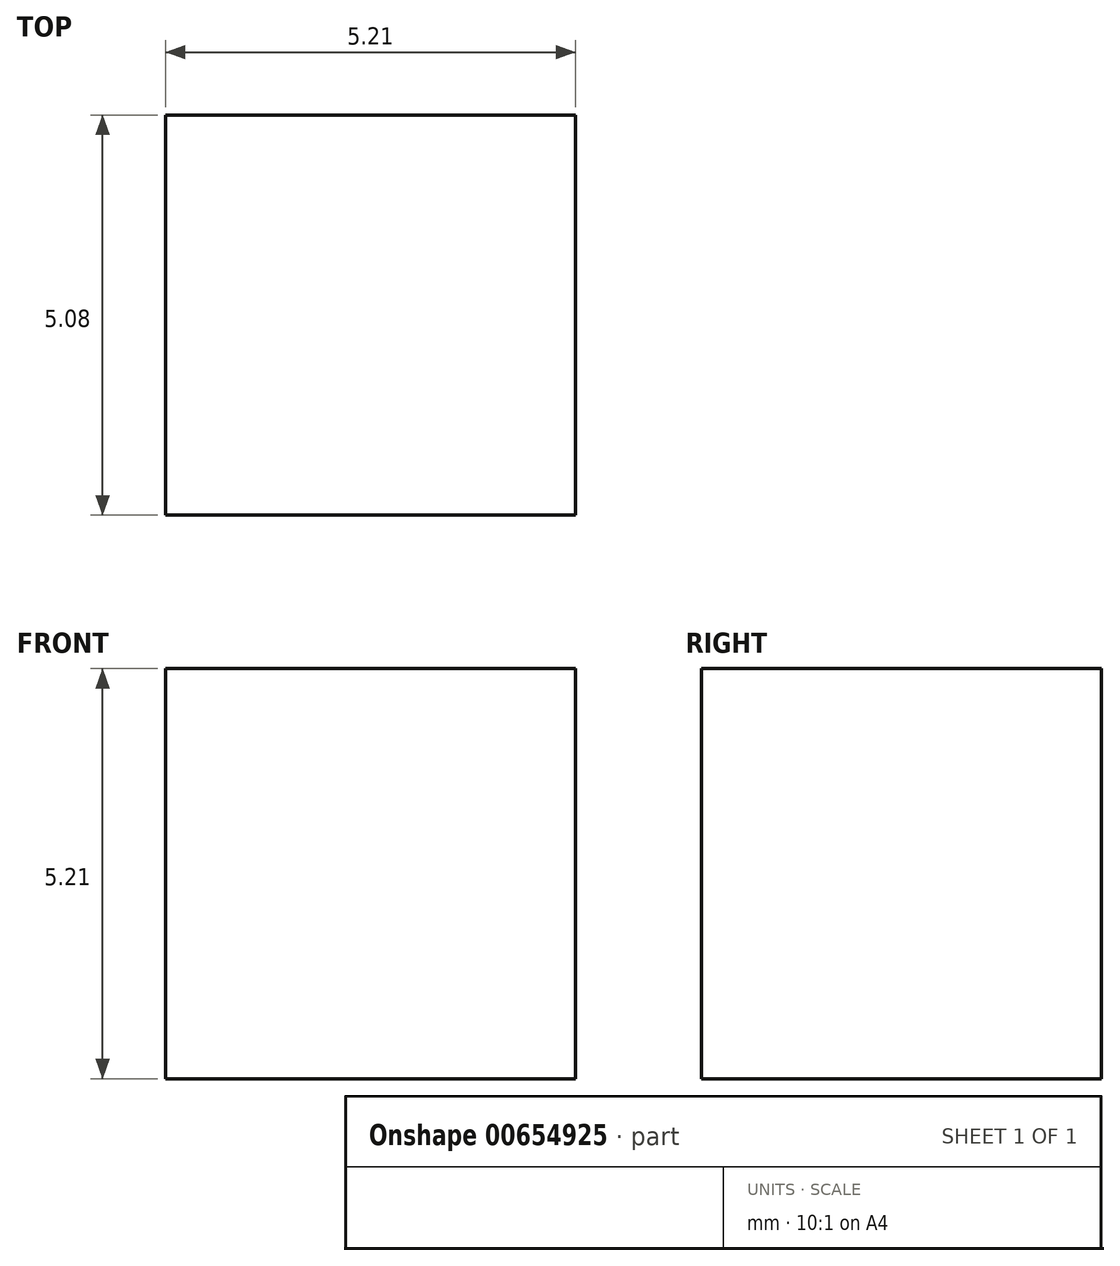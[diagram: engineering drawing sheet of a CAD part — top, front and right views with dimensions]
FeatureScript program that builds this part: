
annotation { "Feature Type Name" : "Feature", "Feature Type Description" : "" }
export const myFeature = defineFeature(function(context is Context, id is Id, definition is map)
    precondition{}
    {
        {
            var Q0;
            Q0=qCreatedBy(makeId("Front.planeOp"),FACE);
            var sketch = newSketch(context, id + "F0", { "sketchPlane" : qUnion([Q0])});
            skLineSegment(sketch, "E0", {"start": v(0, 0) * mm, "end": v(5.2, 0) * mm});
            skLineSegment(sketch, "E1", {"start": v(5.2, 0) * mm, "end": v(5.2, 5.2) * mm});
            skLineSegment(sketch, "E2", {"start": v(5.2, 5.2) * mm, "end": v(0, 5.2) * mm});
            skLineSegment(sketch, "E3", {"start": v(0, 5.2) * mm, "end": v(0, 0) * mm});
            skSolve(sketch);
        }
        {
            var Q0;
            Q0 = qSketchRegion(id + "F0", true);
            extrude(context, id + "F1", {"entities" : qUnion([Q0]), "depth" : 5.08 * mm, "offsetDistance" : 25.4 * mm});
        }
    });
